# Revit family: 632-00-001-DN50-300
name_source: partatom
category: Pipe Accessories
units: mm (PartAtom-declared; Revit-internal decimal feet)

## family parameters
Always vertical = Yes
Cut with Voids When Loaded = No
Part Type = Valve - Breaks Into
Round Connector Dimension = Use Diameter
Shared = No
Work Plane-Based = No

## types (13) — shared parameters
1 = 1 mm  [stored 0.00328084 ft]
2 = 2 mm  [stored 0.00656168 ft]
3 = 3 mm  [stored 0.00984252 ft]
5 = 5 mm  [stored 0.0164042 ft]
6 = 6 mm  [stored 0.019685 ft]
7 = 7 mm  [stored 0.0229659 ft]
DN050-065_PN16 = 632-071-091-006
DN050-080_ PN16 = 632-071-106-006
DN065-080_ PN16 = 632-091-106-006
DN080-100_ PN16 = 632-106-133-006
DN100-125_ PN16 = 632-133-161-006
DN100-150_ PN16 = 632-133-188-006
DN125-150_ PN16 = 632-161-188-006
DN150-200_ PN16 = 632-188-227-006
DN150-225_ PN16 = 632-188-257-006
DN200-225_ PN16 = 632-227-257-006
DN200-250_ PN16 = 632-227-301-006
DN225-250_ PN16 = 632-257-301-006
DN250-300_ PN16 = 632-301-356-006
Description_ = AVK SUPA MAXI™ STEP COUPLING, PN16
Search_table = 632-00-001-DN50-300
URL_product_pages = https://www.avkvalves.com
zero-valued in all types: Default Elevation

## per-type parameters (varying)
| type | Bore | D | D10 | D10_Fastener1 | D10_Fastener11 | DN | D_Fastener1 | D_Fastener11 | Distance | FL_T | Fastener Dis | Fasterner | Fasterner_dia | L | L reference | Rubber | SR1 | SR2 | Taper | Taper1 | Thickness | d1 | distance1 | distance2 |
| DN050-065_PN16 | 25 mm  [stored 0.082021 ft] | 94 mm | 107 mm | 70 mm | 96 mm | 50 mm  [stored 0.164042 ft] | 61 mm | 85 mm | 30 mm  [stored 0.0984252 ft] | 19 mm  [stored 0.062336 ft] | 33 mm | 10 mm  [stored 0.0328084 ft] | 17 mm | 294 mm | 292 mm | 23 mm | 34 mm | 44 mm | 66 mm | 59 mm | 8 mm  [stored 0.0262467 ft] | 10 mm  [stored 0.0328084 ft] | 70 mm | 86 mm |
| DN050-080_ PN16 | 25 mm  [stored 0.082021 ft] | 94 mm | 112 mm | 72 mm | 100 mm | 50 mm  [stored 0.164042 ft] | 61 mm | 85 mm | 30 mm  [stored 0.0984252 ft] | 18 mm  [stored 0.0590551 ft] | 32 mm | 9 mm  [stored 0.0295276 ft] | 16 mm  [stored 0.0524934 ft] | 296 mm | 294 mm | 22 mm  [stored 0.0721785 ft] | 34 mm | 51 mm | 69 mm | 59 mm | 8 mm  [stored 0.0262467 ft] | 10 mm  [stored 0.0328084 ft] | 68 mm | 84 mm |
| DN065-080_ PN16 | 33 mm | 107 mm | 112 mm | 72 mm | 100 mm | 65 mm | 70 mm | 96 mm | 39 mm | 18 mm  [stored 0.0590551 ft] | 32 mm | 9 mm  [stored 0.0295276 ft] | 16 mm  [stored 0.0524934 ft] | 294 mm | 292 mm | 22 mm  [stored 0.0721785 ft] | 44 mm | 51 mm | 69 mm | 59 mm | 8 mm  [stored 0.0262467 ft] | 10 mm  [stored 0.0328084 ft] | 78 mm | 92 mm |
| DN080-100_ PN16 | 40 mm  [stored 0.131234 ft] | 112 mm | 128 mm | 83 mm | 115 mm | 80 mm | 72 mm | 100 mm | 46 mm | 18 mm  [stored 0.0590551 ft] | 32 mm | 9 mm  [stored 0.0295276 ft] | 16 mm  [stored 0.0524934 ft] | 305 mm | 303 mm | 22 mm  [stored 0.0721785 ft] | 51 mm | 65 mm | 79 mm | 61 mm | 10 mm  [stored 0.0328084 ft] | 10 mm  [stored 0.0328084 ft] | 88 mm | 102 mm |
| DN100-125_ PN16 | 50 mm  [stored 0.164042 ft] | 128 mm | 137 mm | 89 mm | 123 mm | 100 mm | 83 mm | 115 mm | 58 mm | 18 mm  [stored 0.0590551 ft] | 32 mm | 9 mm  [stored 0.0295276 ft] | 16 mm  [stored 0.0524934 ft] | 305 mm | 303 mm | 22 mm  [stored 0.0721785 ft] | 65 mm | 78 mm | 85 mm | 61 mm | 10 mm  [stored 0.0328084 ft] | 15 mm  [stored 0.0492126 ft] | 92 mm | 110 mm |
| DN100-150_ PN16 | 50 mm  [stored 0.164042 ft] | 128 mm | 164 mm | 107 mm | 148 mm | 100 mm | 83 mm | 115 mm | 58 mm | 20 mm  [stored 0.0656168 ft] | 35 mm  [stored 0.114829 ft] | 10 mm  [stored 0.0328084 ft] | 18 mm  [stored 0.0590551 ft] | 322 mm | 320 mm | 24 mm  [stored 0.0787402 ft] | 65 mm | 92 mm | 102 mm | 64 mm | 10 mm  [stored 0.0328084 ft] | 15 mm  [stored 0.0492126 ft] | 102 mm | 120 mm |
| DN125-150_ PN16 | 63 mm | 137 mm | 164 mm | 107 mm | 148 mm | 125 mm | 89 mm | 123 mm | 70 mm | 20 mm  [stored 0.0656168 ft] | 35 mm  [stored 0.114829 ft] | 10 mm  [stored 0.0328084 ft] | 18 mm  [stored 0.0590551 ft] | 321 mm | 319 mm | 24 mm  [stored 0.0787402 ft] | 78 mm | 92 mm | 102 mm | 64 mm | 12 mm  [stored 0.0393701 ft] | 15 mm  [stored 0.0492126 ft] | 110 mm | 125 mm |
| DN150-200_ PN16 | 63 mm | 164 mm | 189 mm | 123 mm | 170 mm | 150 mm | 107 mm | 148 mm | 83 mm | 22 mm  [stored 0.0721785 ft] | 39 mm | 11 mm  [stored 0.0360892 ft] | 20 mm  [stored 0.0656168 ft] | 356 mm | 354 mm | 26 mm  [stored 0.0853018 ft] | 92 mm | 112 mm | 117 mm | 71 mm | 14 mm  [stored 0.0459318 ft] | 20 mm  [stored 0.0656168 ft] | 130 mm | 146 mm |
| DN150-225_ PN16 | 75 mm | 164 mm | 213 mm | 138 mm | 191 mm | 150 mm | 107 mm | 148 mm | 83 mm | 24 mm  [stored 0.0787402 ft] | 42 mm  [stored 0.137795 ft] | 12 mm  [stored 0.0393701 ft] | 22 mm  [stored 0.0721785 ft] | 374 mm | 372 mm | 29 mm | 92 mm | 127 mm | 132 mm | 75 mm | 14 mm  [stored 0.0459318 ft] | 20 mm  [stored 0.0656168 ft] | 135 mm | 155 mm |
| DN200-225_ PN16 | 100 mm | 189 mm | 213 mm | 138 mm | 191 mm | 200 mm | 123 mm | 170 mm | 100 mm | 24 mm  [stored 0.0787402 ft] | 42 mm  [stored 0.137795 ft] | 12 mm  [stored 0.0393701 ft] | 22 mm  [stored 0.0721785 ft] | 389 mm | 387 mm | 29 mm | 112 mm | 127 mm | 132 mm | 78 mm | 16 mm  [stored 0.0524934 ft] | 20 mm  [stored 0.0656168 ft] | 152 mm | 170 mm |
| DN200-250_ PN16 | 100 mm | 189 mm | 232 mm | 151 mm | 209 mm | 200 mm | 123 mm | 170 mm | 100 mm | 26 mm  [stored 0.0853018 ft] | 46 mm | 13 mm  [stored 0.0426509 ft] | 23 mm | 386 mm | 384 mm | 31 mm | 112 mm | 149 mm | 144 mm | 77 mm | 16 mm  [stored 0.0524934 ft] | 20 mm  [stored 0.0656168 ft] | 154 mm | 171 mm |
| DN225-250_ PN16 | 113 mm | 213 mm | 232 mm | 151 mm | 209 mm | 225 mm | 138 mm | 191 mm | 114 mm | 26 mm  [stored 0.0853018 ft] | 46 mm | 13 mm  [stored 0.0426509 ft] | 23 mm | 396 mm | 394 mm | 31 mm | 127 mm | 149 mm | 144 mm | 79 mm | 18 mm  [stored 0.0590551 ft] | 25 mm  [stored 0.082021 ft] | 168 mm | 195 mm |
| DN250-300_ PN16 | 125 mm | 232 mm | 267 mm | 173 mm | 240 mm | 250 mm | 151 mm | 209 mm | 134 mm | 28 mm  [stored 0.0918635 ft] | 49 mm  [stored 0.160761 ft] | 14 mm  [stored 0.0459318 ft] | 25 mm  [stored 0.082021 ft] | 437 mm | 435 mm | 34 mm | 149 mm | 176 mm | 165 mm | 87 mm | 20 mm  [stored 0.0656168 ft] | 25 mm  [stored 0.082021 ft] | 200 mm | 228 mm |

note: [stored X ft] marks values corroborated as IEEE doubles in the binary element streams (Revit-internal decimal feet)

## geometry (parser evidence)
native form markers: Sweep x8
no freeform markers — native parametric forms only
